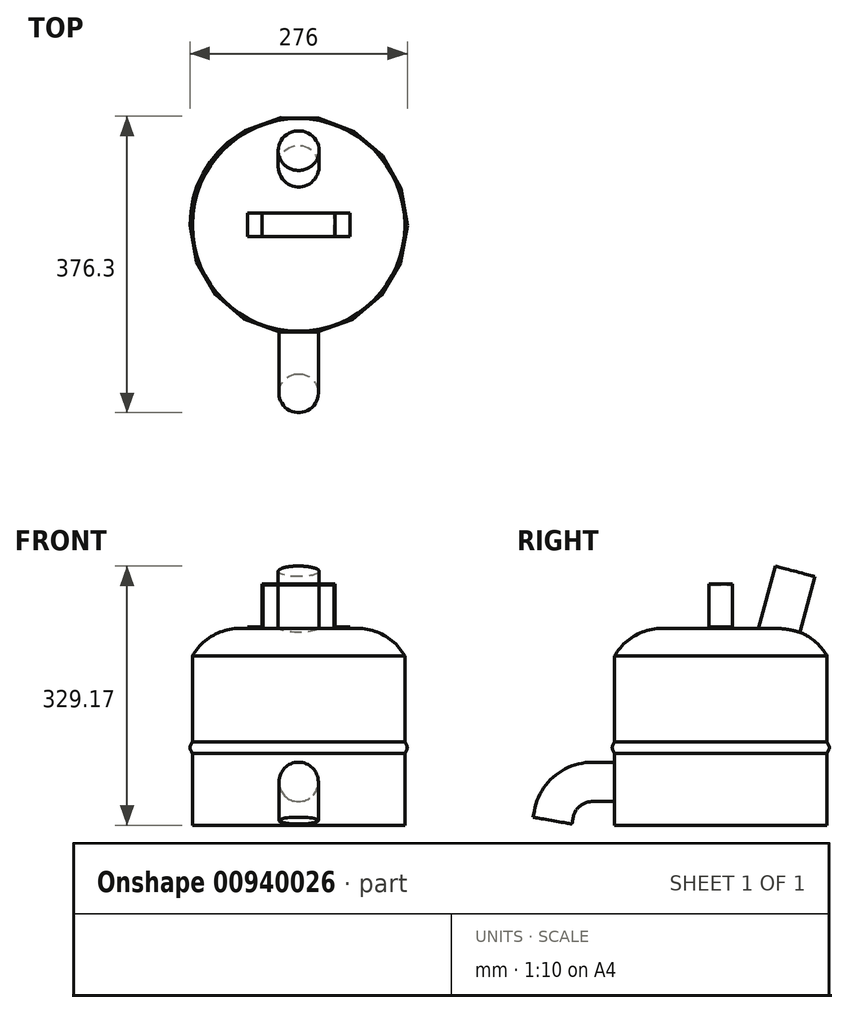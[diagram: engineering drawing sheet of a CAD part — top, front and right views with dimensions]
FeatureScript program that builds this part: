
annotation { "Feature Type Name" : "Feature", "Feature Type Description" : "" }
export const myFeature = defineFeature(function(context is Context, id is Id, definition is map)
    precondition{}
    {
        {
            var Q0;
            Q0=qCreatedBy(makeId("Top.planeOp"),FACE);
            var sketch = newSketch(context, id + "F0", { "sketchPlane" : qUnion([Q0])});
            skCircle(sketch, "E0", {"center": v(0, 0) * mm, "radius": 135 * mm});
            skSolve(sketch);
        }
        {
            var Q0;
            Q0 = qSketchRegion(id + "F0", true);
            extrude(context, id + "F1", {"entities" : qUnion([Q0]), "depth" : 215 * mm, "offsetDistance" : 25 * mm});
        }
        {
            var Q0;
            Q0=qCreatedBy(makeId("Right.planeOp"),FACE);
            var sketch = newSketch(context, id + "F2", { "sketchPlane" : qUnion([Q0])});
            skLineSegment(sketch, "E1.0", {"start": v(-135, 215) * mm, "end": v(135, 215) * mm});
            skPoint(sketch, "E2.0", {"position": v(0, 0) * mm});
            skLineSegment(sketch, "E3", {"start": v(0, 215) * mm, "end": v(0, 250) * mm});
            skLineSegment(sketch, "E4", {"start": v(0, 250) * mm, "end": v(-75, 250) * mm});
            skArc(sketch, "E5", {"start": v(-75, 250) * mm, "mid": v(-109.65, 240.47) * mm, "end": v(-135, 215) * mm});
            skSolve(sketch);
        }
        {
            var Q0;
            Q0 = qSketchRegion(id + "F2", true);
            var Q1;
            Q1=sQuery(id+"F2.wireOp",EDGE,"E3");
            revolve(context, id + "F3", {"operationType" : NewBodyOperationType.ADD, "surfaceOperationType" : NewSurfaceOperationType.NEW, "entities" : qUnion([Q0]), "axis" : qUnion([Q1]), "revolveType" : RevolveType.FULL});
        }
        {
            var Q0;
            Q0=qCreatedBy(makeId("Front.planeOp"),FACE);
            var sketch = newSketch(context, id + "F4", { "sketchPlane" : qUnion([Q0])});
            skLineSegment(sketch, "E6.0", {"start": v(75, 250) * mm, "end": v(-75, 250) * mm, "construction": true});
            skLineSegment(sketch, "E7", {"start": v(-65, 250) * mm, "end": v(-45, 250) * mm});
            skLineSegment(sketch, "E8", {"start": v(-45, 250) * mm, "end": v(-45, 305) * mm});
            skLineSegment(sketch, "E9", {"start": v(-45, 305) * mm, "end": v(0, 305) * mm});
            skLineSegment(sketch, "E10.0", {"start": v(-46.5, 306.5) * mm, "end": v(0, 306.5) * mm});
            skLineSegment(sketch, "E11.0", {"start": v(-46.5, 251.5) * mm, "end": v(-46.5, 306.5) * mm});
            skLineSegment(sketch, "E12.0", {"start": v(-65, 251.5) * mm, "end": v(-46.5, 251.5) * mm});
            skLineSegment(sketch, "E13", {"start": v(-65, 251.5) * mm, "end": v(-65, 250) * mm});
            skLineSegment(sketch, "E14", {"start": v(0, 306.5) * mm, "end": v(0, 305) * mm});
            skSolve(sketch);
        }
        {
            var Q0;
            Q0 = qSketchRegion(id + "F4", true);
            extrude(context, id + "F5", {"entities" : qUnion([Q0]), "depth" : 30 * mm, "offsetDistance" : 25 * mm, "symmetric" : true});
        }
        {
            var Q0;
            Q0=makeQuery(id+"F5.opExtrude","SWEPT_BODY",BODY,{"disambiguationData":[OSD([sQuery(id+"F4.wireOp",EDGE,"E7"),sQuery(id+"F4.wireOp",EDGE,"E8"),sQuery(id+"F4.wireOp",EDGE,"E9"),sQuery(id+"F4.wireOp",EDGE,"E10.0"),sQuery(id+"F4.wireOp",EDGE,"E11.0"),sQuery(id+"F4.wireOp",EDGE,"E12.0"),sQuery(id+"F4.wireOp",EDGE,"E13"),sQuery(id+"F4.wireOp",EDGE,"E14")])]});
            var Q1;
            Q1=qCreatedBy(makeId("Right.planeOp"),FACE);
            mirror(context, id + "F6", {"operationType" : NewBodyOperationType.ADD, "entities" : qUnion([Q0]), "mirrorPlane" : qUnion([Q1])});
        }
        {
            var Q0;
            Q0=qCreatedBy(makeId("Right.planeOp"),FACE);
            var sketch = newSketch(context, id + "F7", { "sketchPlane" : qUnion([Q0])});
            skArc(sketch, "E15", {"start": v(135, 215) * mm, "mid": v(109.65, 240.47) * mm, "end": v(75, 250) * mm, "construction": true});
            skLineSegment(sketch, "E16", {"start": v(79.9, 268.32) * mm, "end": v(75, 250) * mm});
            skLineSegment(sketch, "E17", {"start": v(75, 250) * mm, "end": v(75, 270.79) * mm, "construction": true});
            skSolve(sketch);
        }
        {
            var Q0;
            Q0=sQuery(id+"F7.wireOp",EDGE,"E15");
            cPlane(context, id + "F8", {"entities" : qUnion([Q0]), "cplaneType" : CPlaneType.LINE_ANGLE, "offset" : 25 * mm, "angle" : 75 * degree, "width" : 150 * mm, "height" : 150 * mm});
        }
        {
            var Q0;
            Q0=qCreatedBy(id+"F8.planeOp",FACE);
            var Q1;
            Q1=sQuery(id+"F7.wireOp",VERTEX,"E15.end");
            cPlane(context, id + "F9", {"entities" : qUnion([Q0, Q1]), "cplaneType" : CPlaneType.PLANE_POINT, "offset" : 25 * mm, "width" : 150 * mm, "height" : 150 * mm});
        }
        {
            var Q0;
            Q0=qCreatedBy(id+"F9.planeOp",FACE);
            var sketch = newSketch(context, id + "F10", { "sketchPlane" : qUnion([Q0])});
            skPoint(sketch, "E18.0", {"position": v(0, 7.74) * mm});
            skCircle(sketch, "E19", {"center": v(0, 7.74) * mm, "radius": 26 * mm});
            skSolve(sketch);
        }
        {
            var Q0;
            Q0 = qSketchRegion(id + "F10", true);
            extrude(context, id + "F11", {"entities" : qUnion([Q0]), "operationType" : NewBodyOperationType.ADD, "depth" : 150 * mm, "offsetDistance" : 25 * mm, "symmetric" : true});
        }
        {
            var Q0;
            Q0=qCreatedBy(makeId("Front.planeOp"),FACE);
            cPlane(context, id + "F12", {"entities" : qUnion([Q0]), "cplaneType" : CPlaneType.OFFSET, "offset" : 135 * mm, "width" : 150 * mm, "height" : 150 * mm});
        }
        {
            var Q0;
            Q0=qCreatedBy(id+"F12.planeOp",FACE);
            var sketch = newSketch(context, id + "F13", { "sketchPlane" : qUnion([Q0])});
            skPoint(sketch, "E20", {"position": v(0, 55) * mm});
            skCircle(sketch, "E21", {"center": v(0, 55) * mm, "radius": 25 * mm});
            skSolve(sketch);
        }
        {
            var Q0;
            Q0=qCreatedBy(makeId("Right.planeOp"),FACE);
            var sketch = newSketch(context, id + "F14", { "sketchPlane" : qUnion([Q0])});
            skPoint(sketch, "E22.0", {"position": v(-135, 55) * mm});
            skLineSegment(sketch, "E23", {"start": v(-135, 55) * mm, "end": v(-163.05, 55) * mm});
            skLineSegment(sketch, "E24", {"start": v(-212.29, 13.68) * mm, "end": v(-213.68, 5.76) * mm});
            skPoint(sketch, "E25.visualSharp", {"position": v(-205, 55) * mm});
            skArc(sketch, "E25.filletArc", {"start": v(-163.05, 55) * mm, "mid": v(-195.18, 43.3) * mm, "end": v(-212.29, 13.68) * mm});
            skSolve(sketch);
        }
        {
            var Q0;
            Q0=makeQuery(id+"F13.imprint","IMPRINT",FACE,{"disambiguationData":[TD([[makeQuery(id+"F13.imprint","IMPRINT",EDGE,{"derivedFrom":sQuery(id+"F13.wireOp",EDGE,"E21")}),1.0]])]});
            var Q1;
            Q1=sQuery(id+"F14.wireOp",EDGE,"E25.filletArc");
            var Q2;
            Q2=sQuery(id+"F14.wireOp",EDGE,"E24");
            var Q3;
            Q3=sQuery(id+"F14.wireOp",EDGE,"E23");
            sweep(context, id + "F15", {"profiles" : qUnion([Q0]), "path" : qUnion([Q1, Q2, Q3])});
        }
        {
            var Q0;
            Q0=qCreatedBy(makeId("Front.planeOp"),FACE);
            var sketch = newSketch(context, id + "F16", { "sketchPlane" : qUnion([Q0])});
            skLineSegment(sketch, "E26", {"start": v(135, 106) * mm, "end": v(135, 91) * mm});
            skLineSegment(sketch, "E27", {"start": v(0, 0) * mm, "end": v(135, 0) * mm, "construction": true});
            skLineSegment(sketch, "E28", {"start": v(135, 91) * mm, "end": v(137.53, 96.37) * mm});
            skLineSegment(sketch, "E29", {"start": v(135, 106) * mm, "end": v(137.53, 100.63) * mm});
            skArc(sketch, "E30", {"start": v(137.53, 96.37) * mm, "mid": v(138, 98.5) * mm, "end": v(137.53, 100.63) * mm});
            skLineSegment(sketch, "E31", {"start": v(135, 106) * mm, "end": v(133, 98.5) * mm, "construction": true});
            skLineSegment(sketch, "E32", {"start": v(133, 98.5) * mm, "end": v(135, 91) * mm, "construction": true});
            skSolve(sketch);
        }
        {
            var Q0;
            Q0=makeQuery(id+"F16.imprint","IMPRINT",FACE,{"disambiguationData":[TD([[makeQuery(id+"F16.imprint","IMPRINT",EDGE,{"derivedFrom":sQuery(id+"F16.wireOp",EDGE,"E26")}),1.0]])]});
            var Q1;
            Q1=makeQuery(id+"F1.opExtrude","CAP_EDGE",EDGE,{"disambiguationData":[OSD([sQuery(id+"F0.wireOp",EDGE,"E0")])],"isStart":true});
            revolve(context, id + "F17", {"operationType" : NewBodyOperationType.ADD, "surfaceOperationType" : NewSurfaceOperationType.NEW, "entities" : qUnion([Q0]), "axis" : qUnion([Q1]), "revolveType" : RevolveType.FULL});
        }
    });
